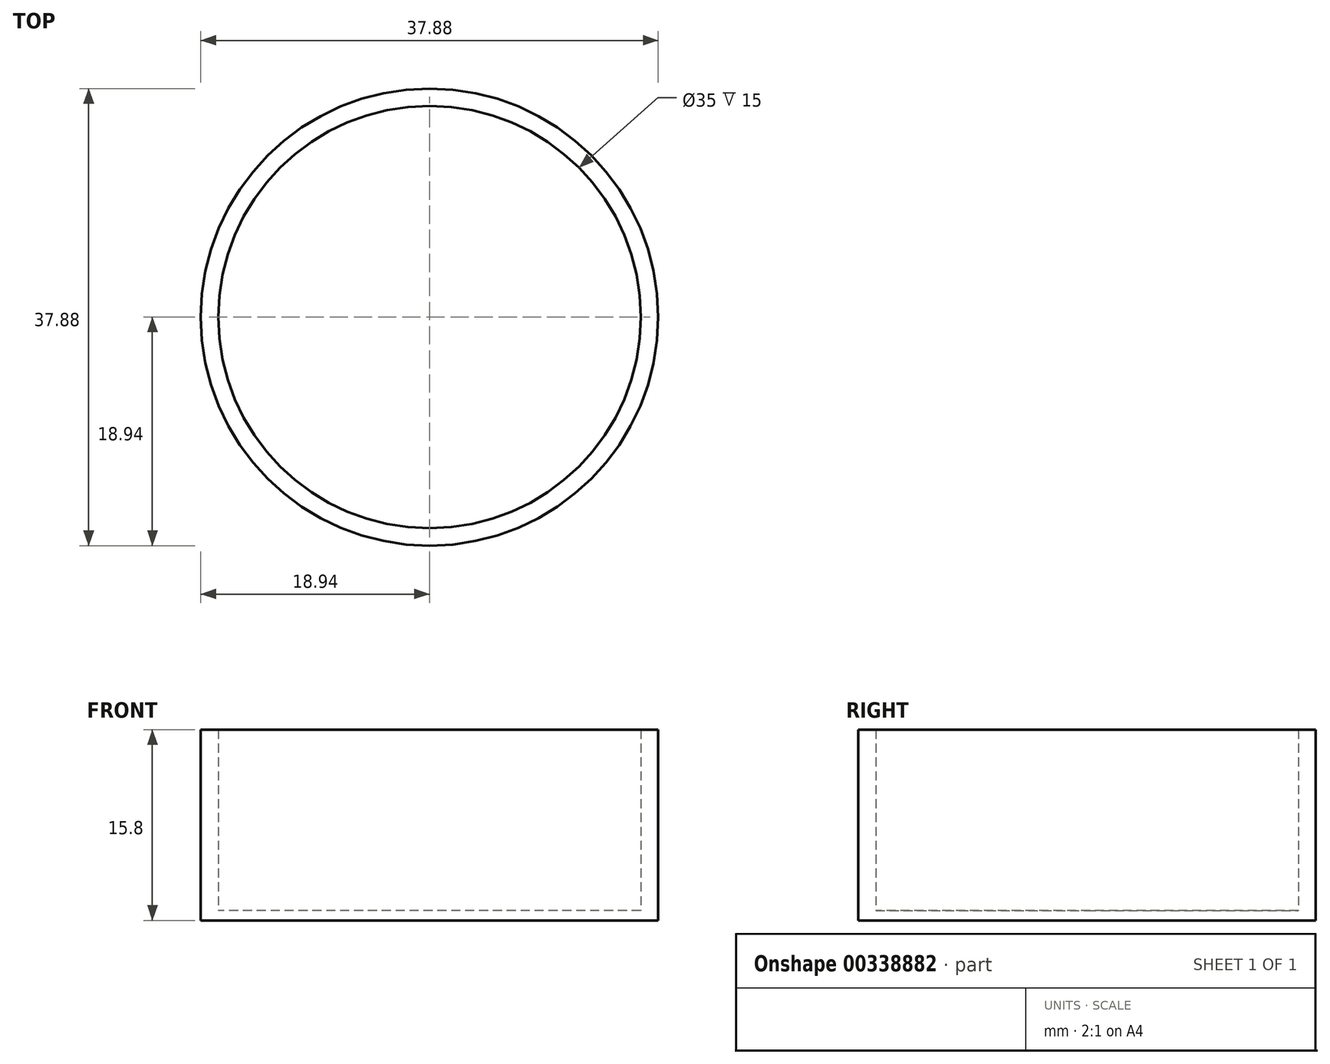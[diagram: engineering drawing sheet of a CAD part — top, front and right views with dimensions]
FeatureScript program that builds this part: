
annotation { "Feature Type Name" : "Feature", "Feature Type Description" : "" }
export const myFeature = defineFeature(function(context is Context, id is Id, definition is map)
    precondition{}
    {
        {
            var Q0;
            Q0=qCreatedBy(makeId("Top.planeOp"),FACE);
            var sketch = newSketch(context, id + "F0", { "sketchPlane" : qUnion([Q0])});
            skCircle(sketch, "E0", {"center": v(0, 0) * mm, "radius": 18.94 * mm});
            skSolve(sketch);
        }
        {
            var Q0;
            Q0 = qSketchRegion(id + "F0", true);
            extrude(context, id + "F1", {"entities" : qUnion([Q0]), "depth" : (.2 * 4) * mm});
        }
        {
            var Q0;
            Q0=makeQuery(id+"F1.opExtrude","CAP_FACE",FACE,{"disambiguationData":[OSD([sQuery(id+"F0.wireOp",EDGE,"E0")])],"isStart":false});
            var sketch = newSketch(context, id + "F2", { "sketchPlane" : qUnion([Q0])});
            skCircle(sketch, "E1.0.0", {"center": v(0, 0) * mm, "radius": 18.94 * mm});
            skCircle(sketch, "E2.0", {"center": v(0, 0) * mm, "radius": 17.5 * mm});
            skSolve(sketch);
        }
        {
            var Q0;
            Q0 = qSketchRegion(id + "F2", true);
            extrude(context, id + "F3", {"entities" : qUnion([Q0]), "operationType" : NewBodyOperationType.ADD, "depth" : 15 * mm});
        }
    });
